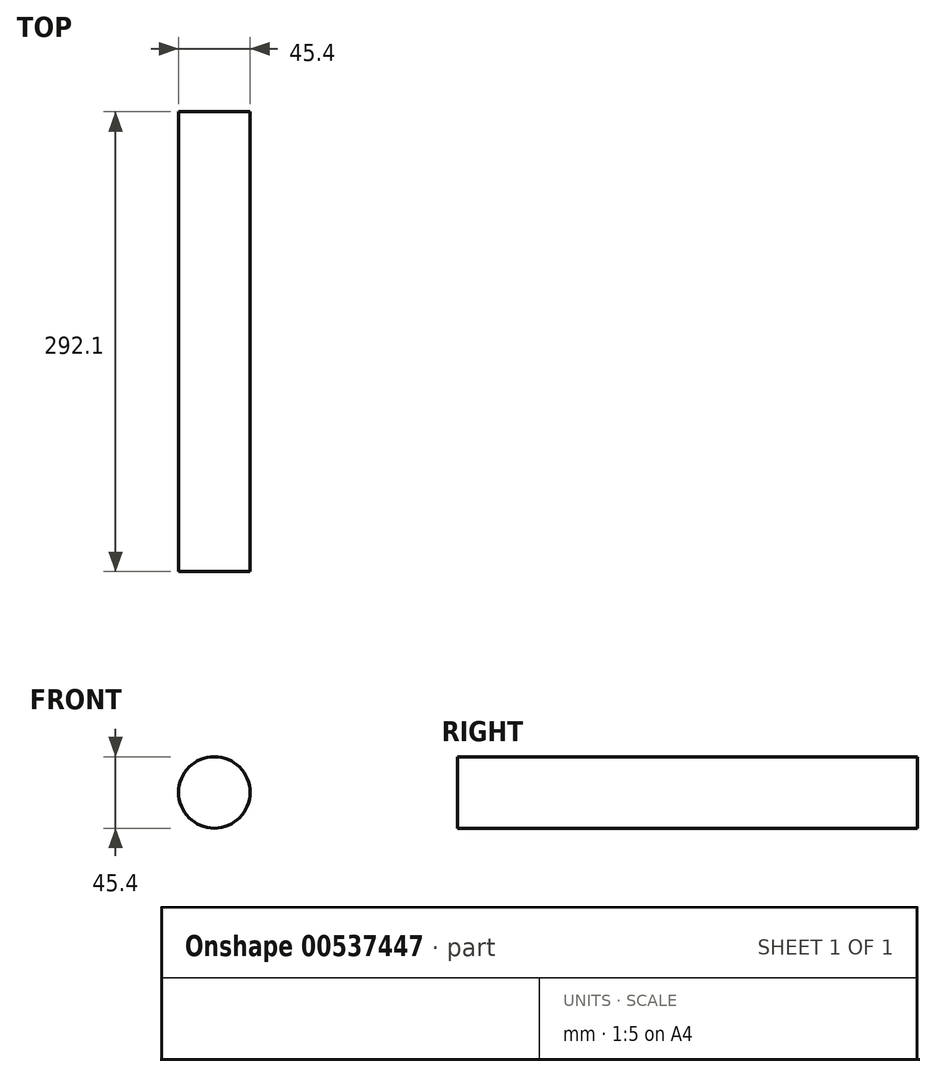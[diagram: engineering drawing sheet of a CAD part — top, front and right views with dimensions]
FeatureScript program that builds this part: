
annotation { "Feature Type Name" : "Feature", "Feature Type Description" : "" }
export const myFeature = defineFeature(function(context is Context, id is Id, definition is map)
    precondition{}
    {
        {
            var Q0;
            Q0=qCreatedBy(makeId("Front.planeOp"),FACE);
            var sketch = newSketch(context, id + "F0", { "sketchPlane" : qUnion([Q0])});
            skCircle(sketch, "E0", {"center": v(-8.92, 6.9) * mm, "radius": 22.7 * mm});
            skSolve(sketch);
        }
        {
            var Q0;
            Q0=makeQuery(id+"F0.imprint","IMPRINT",FACE,{"disambiguationData":[TD([[makeQuery(id+"F0.imprint","IMPRINT",EDGE,{"derivedFrom":sQuery(id+"F0.wireOp",EDGE,"E0")}),1.0]])]});
            extrude(context, id + "F1", {"entities" : qUnion([Q0]), "depth" : 25.4 * mm, "offsetDistance" : 25.4 * mm});
        }
        {
            var Q0;
            Q0=makeQuery(id+"F1.opExtrude","CAP_FACE",FACE,{"disambiguationData":[OSD([sQuery(id+"F0.wireOp",EDGE,"E0")])],"isStart":true});
            extrude(context, id + "F2", {"entities" : qUnion([Q0]), "operationType" : NewBodyOperationType.ADD, "depth" : 266.7 * mm, "offsetDistance" : 25.4 * mm});
        }
    });
